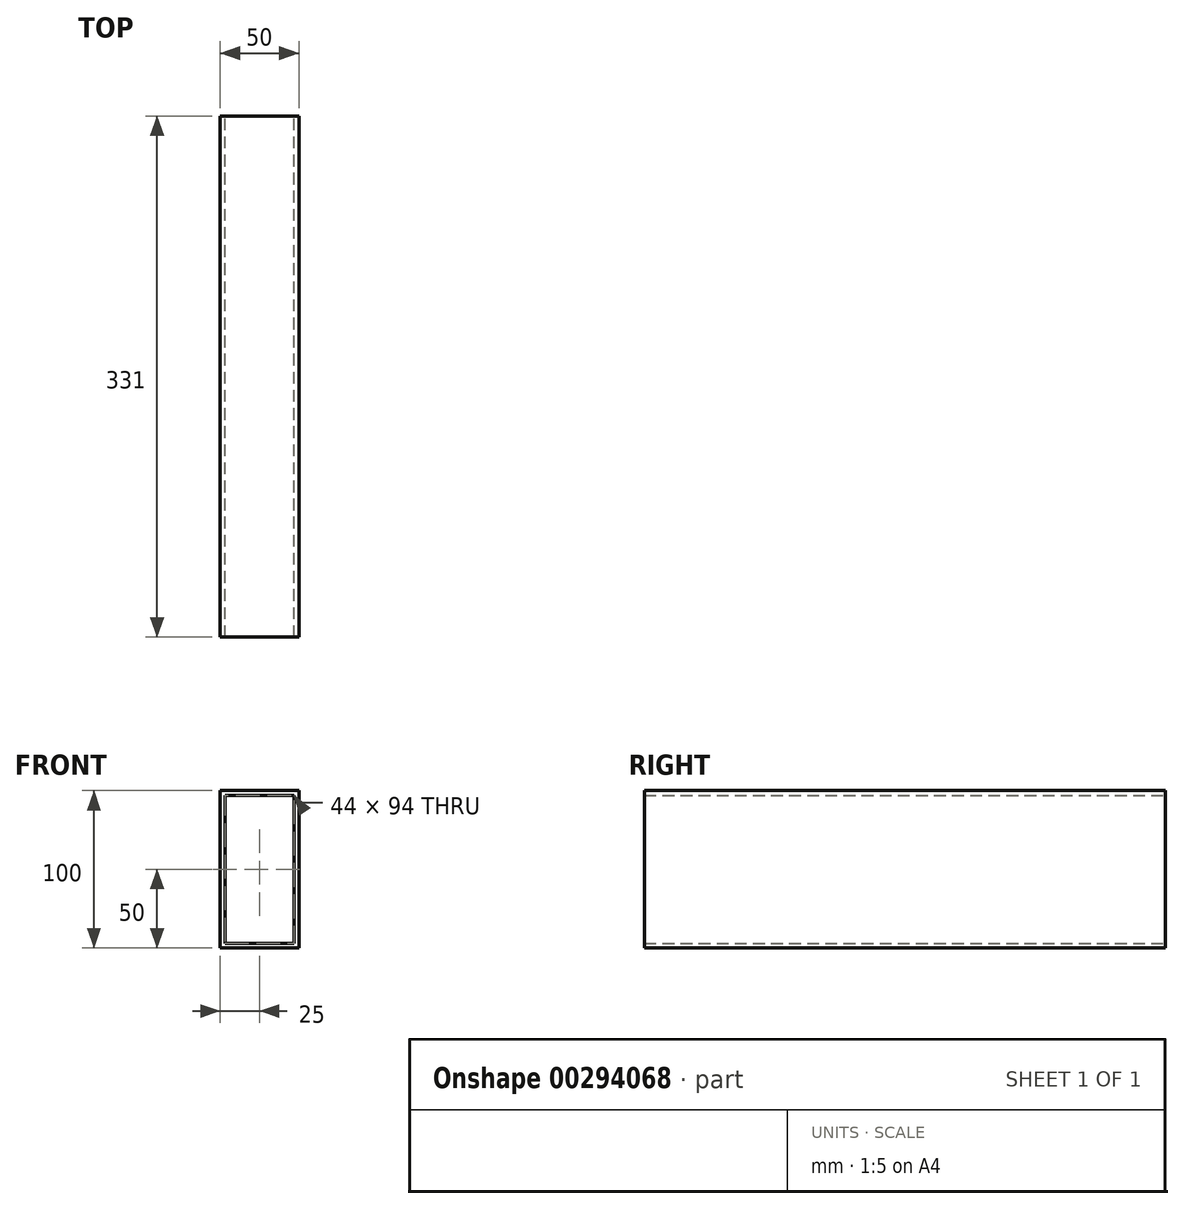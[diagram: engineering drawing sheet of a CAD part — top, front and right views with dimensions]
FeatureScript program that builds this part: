
annotation { "Feature Type Name" : "Feature", "Feature Type Description" : "" }
export const myFeature = defineFeature(function(context is Context, id is Id, definition is map)
    precondition{}
    {
        {
            var Q0;
            Q0=qCreatedBy(makeId("Front.planeOp"),FACE);
            var sketch = newSketch(context, id + "F0", { "sketchPlane" : qUnion([Q0])});
            skLineSegment(sketch, "E0", {"start": v(0, 0) * mm, "end": v(0, 100) * mm});
            skLineSegment(sketch, "E1", {"start": v(0, 100) * mm, "end": v(50, 100) * mm});
            skLineSegment(sketch, "E2", {"start": v(50, 100) * mm, "end": v(50, 0) * mm});
            skLineSegment(sketch, "E3", {"start": v(50, 0) * mm, "end": v(0, 0) * mm});
            skLineSegment(sketch, "E4", {"start": v(3, 97) * mm, "end": v(3, 3) * mm});
            skLineSegment(sketch, "E5", {"start": v(3, 3) * mm, "end": v(47, 3) * mm});
            skLineSegment(sketch, "E6", {"start": v(47, 3) * mm, "end": v(47, 97) * mm});
            skLineSegment(sketch, "E7", {"start": v(3, 97) * mm, "end": v(47, 97) * mm});
            skSolve(sketch);
        }
        {
            var Q0;
            Q0=makeQuery(id+"F0.imprint","IMPRINT",FACE,{"disambiguationData":[TD([[makeQuery(id+"F0.imprint","IMPRINT",EDGE,{"derivedFrom":sQuery(id+"F0.wireOp",EDGE,"E0")}),-1.0]])]});
            extrude(context, id + "F1", {"entities" : qUnion([Q0]), "depth" : 331 * mm});
        }
    });
